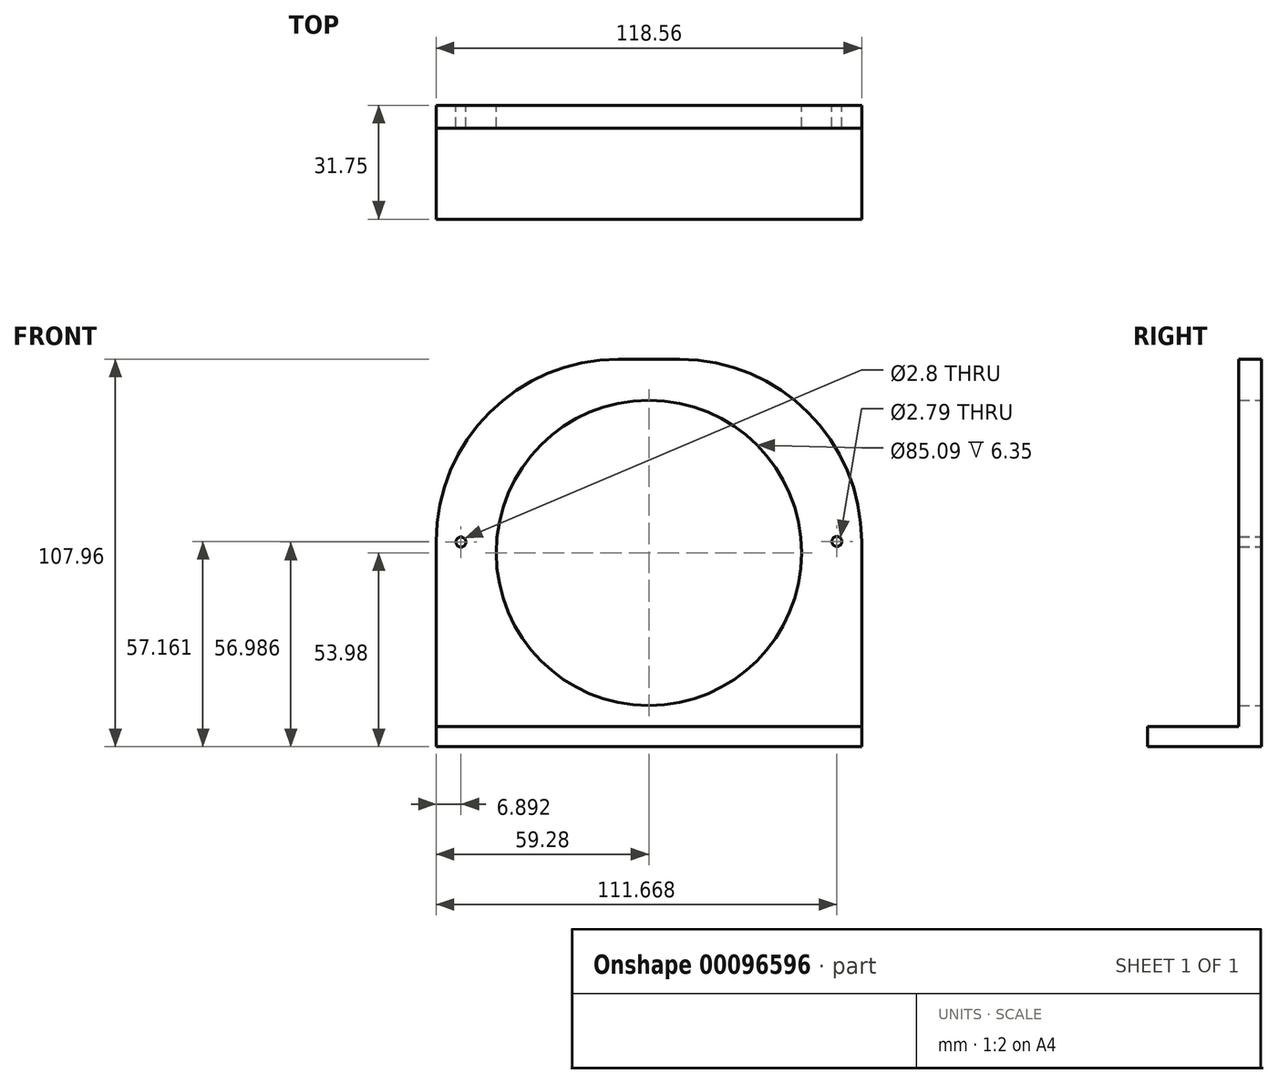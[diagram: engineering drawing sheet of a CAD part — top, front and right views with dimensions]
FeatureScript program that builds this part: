
annotation { "Feature Type Name" : "Feature", "Feature Type Description" : "" }
export const myFeature = defineFeature(function(context is Context, id is Id, definition is map)
    precondition{}
    {
        {
            var Q0;
            Q0=qCreatedBy(makeId("Front.planeOp"),FACE);
            var sketch = newSketch(context, id + "F0", { "sketchPlane" : qUnion([Q0])});
            skCircle(sketch, "E0", {"center": v(0, 0) * mm, "radius": 42.55 * mm});
            skLineSegment(sketch, "E1", {"start": v(0, 0) * mm, "end": v(0, -53.98) * mm});
            skLineSegment(sketch, "E2", {"start": v(0, -53.98) * mm, "end": v(0, 0) * mm});
            skLineSegment(sketch, "E3", {"start": v(0, 0) * mm, "end": v(52.39, 0) * mm});
            skLineSegment(sketch, "E4", {"start": v(0, 0) * mm, "end": v(-52.39, 0) * mm});
            skLineSegment(sketch, "E5", {"start": v(-52.39, 0) * mm, "end": v(0, 0) * mm});
            skLineSegment(sketch, "E6", {"start": v(-52.39, 0) * mm, "end": v(-52.39, 3) * mm});
            skLineSegment(sketch, "E7", {"start": v(-52.39, 3) * mm, "end": v(-52.39, 0) * mm});
            skLineSegment(sketch, "E8", {"start": v(52.39, 0) * mm, "end": v(52.39, 3.18) * mm});
            skLineSegment(sketch, "E9", {"start": v(52.39, 3.18) * mm, "end": v(52.39, 0) * mm});
            skCircle(sketch, "E10", {"center": v(-52.39, 3) * mm, "radius": 1.4 * mm});
            skCircle(sketch, "E11", {"center": v(52.39, 3.18) * mm, "radius": 1.4 * mm});
            skLineSegment(sketch, "E12.bottom", {"start": v(59.28, -53.98) * mm, "end": v(-59.28, -53.98) * mm});
            skLineSegment(sketch, "E12.top", {"start": v(59.28, 53.98) * mm, "end": v(-59.28, 53.98) * mm});
            skLineSegment(sketch, "E12.left", {"start": v(59.28, -53.98) * mm, "end": v(59.28, 53.98) * mm});
            skLineSegment(sketch, "E12.right", {"start": v(-59.28, -53.98) * mm, "end": v(-59.28, 53.98) * mm});
            skSolve(sketch);
        }
        {
            var Q0;
            Q0 = qSketchRegion(id + "F0", true);
            extrude(context, id + "F1", {"entities" : qUnion([Q0]), "depth" : 6.35 * mm});
        }
        {
            var Q0;
            Q0=makeQuery(id+"F1.opExtrude","SWEPT_EDGE",EDGE,{"disambiguationData":[OSD([sQuery(id+"F0.wireOp",EDGE,"E12.top"),sQuery(id+"F0.wireOp",EDGE,"E12.left")])]});
            var Q1;
            Q1=makeQuery(id+"F1.opExtrude","SWEPT_EDGE",EDGE,{"disambiguationData":[OSD([sQuery(id+"F0.wireOp",EDGE,"E12.top"),sQuery(id+"F0.wireOp",EDGE,"E12.right")])]});
            fillet(context, id + "F2", {"entities" : qUnion([Q0, Q1]), "radius" : 50.8 * mm, "tangentPropagation" : true, "allowEdgeOverflow" : false});
        }
        {
            var Q0;
            Q0=makeQuery(id+"F1.opExtrude","CAP_FACE",FACE,{"disambiguationData":[OSD([sQuery(id+"F0.wireOp",EDGE,"E0"),sQuery(id+"F0.wireOp",EDGE,"E10"),sQuery(id+"F0.wireOp",EDGE,"E11"),sQuery(id+"F0.wireOp",EDGE,"E12.bottom"),sQuery(id+"F0.wireOp",EDGE,"E12.top"),sQuery(id+"F0.wireOp",EDGE,"E12.left"),sQuery(id+"F0.wireOp",EDGE,"E12.right")])],"isStart":false});
            var sketch = newSketch(context, id + "F3", { "sketchPlane" : qUnion([Q0])});
            skLineSegment(sketch, "E13.bottom", {"start": v(-59.28, -53.98) * mm, "end": v(59.28, -53.98) * mm});
            skLineSegment(sketch, "E13.top", {"start": v(-59.28, -48.36) * mm, "end": v(59.28, -48.36) * mm});
            skLineSegment(sketch, "E13.left", {"start": v(-59.28, -53.98) * mm, "end": v(-59.28, -48.36) * mm});
            skLineSegment(sketch, "E13.right", {"start": v(59.28, -53.98) * mm, "end": v(59.28, -48.36) * mm});
            skSolve(sketch);
        }
        {
            var Q0;
            Q0 = qSketchRegion(id + "F3", true);
            extrude(context, id + "F4", {"entities" : qUnion([Q0]), "operationType" : NewBodyOperationType.ADD, "depth" : 25.4 * mm});
        }
    });
